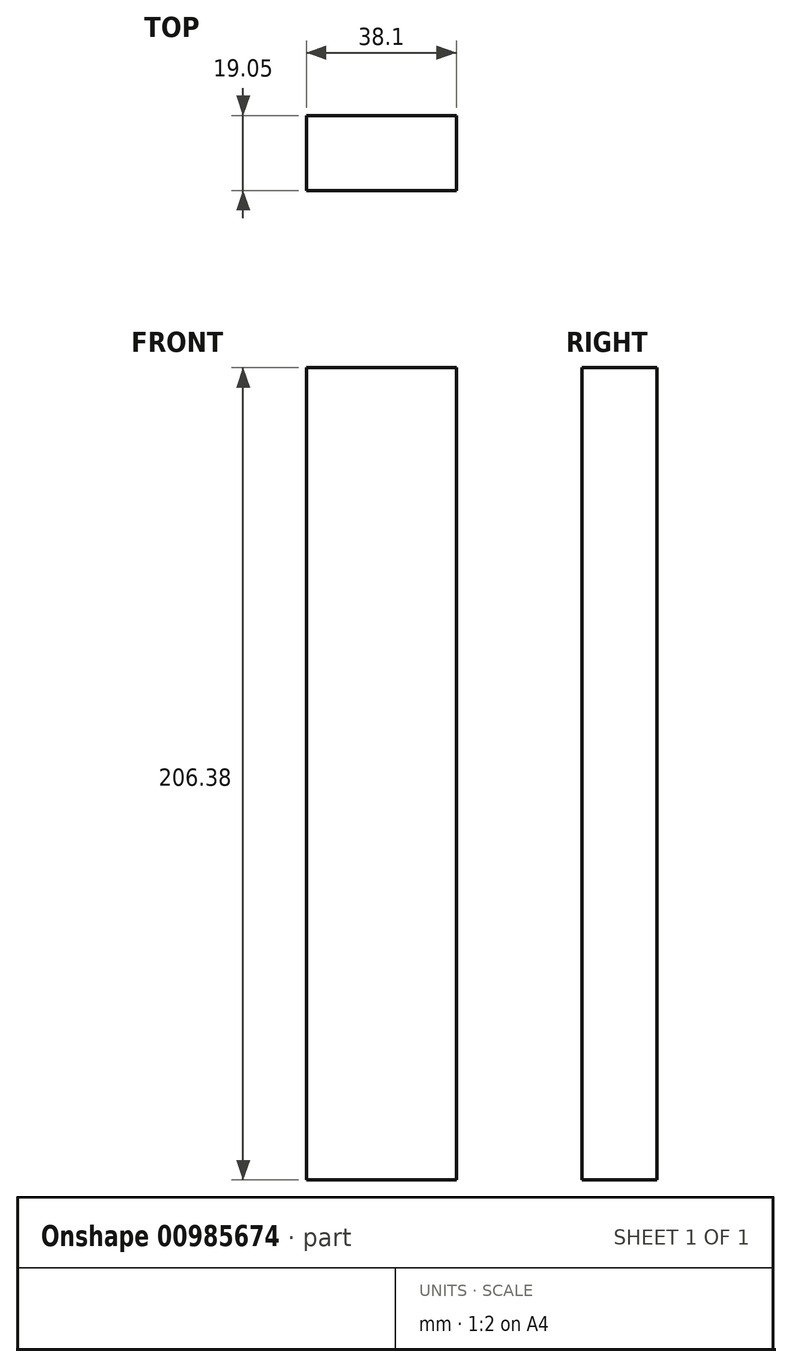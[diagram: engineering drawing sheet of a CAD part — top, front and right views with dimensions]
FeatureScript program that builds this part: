
annotation { "Feature Type Name" : "Feature", "Feature Type Description" : "" }
export const myFeature = defineFeature(function(context is Context, id is Id, definition is map)
    precondition{}
    {
        {
            var Q0;
            Q0=qCreatedBy(makeId("Front.planeOp"),FACE);
            var sketch = newSketch(context, id + "F0", { "sketchPlane" : qUnion([Q0])});
            skLineSegment(sketch, "E0.bottom", {"start": v(19.05, 103.19) * mm, "end": v(-19.05, 103.19) * mm});
            skLineSegment(sketch, "E0.top", {"start": v(19.05, -103.19) * mm, "end": v(-19.05, -103.19) * mm});
            skLineSegment(sketch, "E0.left", {"start": v(19.05, 103.19) * mm, "end": v(19.05, -103.19) * mm});
            skLineSegment(sketch, "E0.right", {"start": v(-19.05, 103.19) * mm, "end": v(-19.05, -103.19) * mm});
            skPoint(sketch, "E0.middle", {"position": v(0, 0) * mm});
            skSolve(sketch);
        }
        {
            var Q0;
            Q0 = qSketchRegion(id + "F0", true);
            extrude(context, id + "F1", {"entities" : qUnion([Q0]), "depth" : 19.05 * mm, "offsetDistance" : 25.4 * mm});
        }
    });
